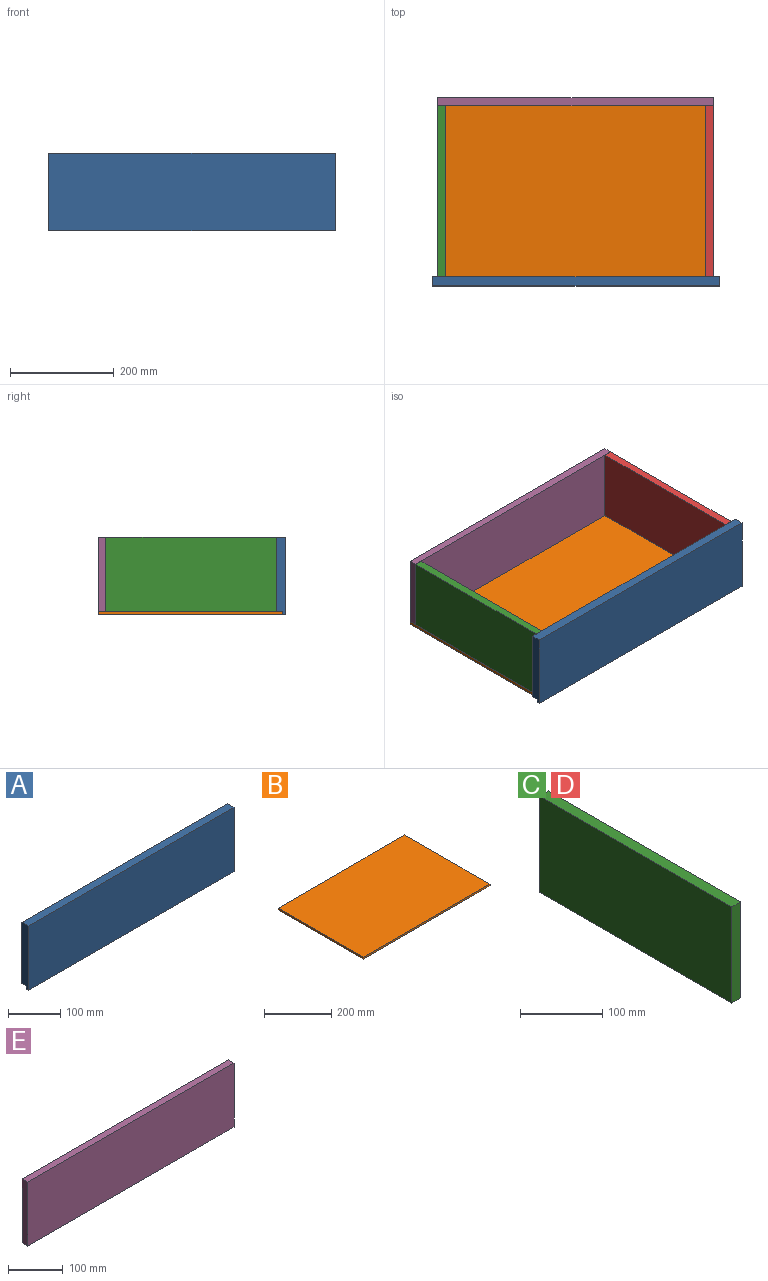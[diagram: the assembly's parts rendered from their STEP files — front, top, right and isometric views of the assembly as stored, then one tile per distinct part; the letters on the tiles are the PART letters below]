
ASSEMBLY  parts=5 mates=4
PART A: 8 faces, bbox 554x18x150 mm
  f0: plane 554x143mm, normal (0,1,0), area 79222mm2, adj f1,f2,f4,f6
  f1: plane 554x18mm, normal (0,0,1), area 9972mm2, adj f0,f2,f4,f5
  f2: plane 150x18mm, normal (-1,0,0), area 2616mm2, adj f0,f1,f3,f5,f6,f7
  f3: plane 554x6mm, normal (0,0,-1), area 3324mm2, adj f2,f4,f5,f7
  f4: plane 150x18mm, normal (1,0,0), area 2616mm2, adj f0,f1,f3,f5,f6,f7
  f5: plane 554x150mm, normal (0,-1,0), area 83100mm2, adj f1,f2,f3,f4
  f6: plane 554x12mm, normal (0,0,-1), area 6648mm2, adj f0,f2,f4,f7
  f7: plane 554x7mm, normal (0,1,0), area 3878mm2, adj f2,f3,f4,f6
PART B: 6 faces, bbox 532.5x357x6.5 mm
  f0: plane 532.5x6.5mm, normal (0,1,0), area 3461.2mm2, adj f1,f3,f4,f5
  f1: plane 357x6.5mm, normal (-1,0,0), area 2320.5mm2, adj f0,f2,f4,f5
  f2: plane 532.5x6.5mm, normal (0,-1,0), area 3461.2mm2, adj f1,f3,f4,f5
  f3: plane 357x6.5mm, normal (1,0,0), area 2320.5mm2, adj f0,f2,f4,f5
  f4: plane 532.5x357mm, normal (0,0,1), area 190102.5mm2, adj f0,f1,f2,f3
  f5: plane 532.5x357mm, normal (0,0,-1), area 190102.5mm2, adj f0,f1,f2,f3
PART C: 6 faces, bbox 15x330x143 mm
  f0: plane 330x15mm, normal (0,0,1), area 4950mm2, adj f1,f3,f4,f5
  f1: plane 143x15mm, normal (0,-1,0), area 2145mm2, adj f0,f2,f4,f5
  f2: plane 330x15mm, normal (0,0,-1), area 4950mm2, adj f1,f3,f4,f5
  f3: plane 143x15mm, normal (0,1,0), area 2145mm2, adj f0,f2,f4,f5
  f4: plane 330x143mm, normal (1,0,0), area 47190mm2, adj f0,f1,f2,f3
  f5: plane 330x143mm, normal (-1,0,0), area 47190mm2, adj f0,f1,f2,f3
PART D: same geometry as C
PART E: 6 faces, bbox 532.5x15x143 mm
  f0: plane 532.5x15mm, normal (0,0,1), area 7987.5mm2, adj f1,f3,f4,f5
  f1: plane 143x15mm, normal (-1,0,0), area 2145mm2, adj f0,f2,f4,f5
  f2: plane 532.5x15mm, normal (0,0,-1), area 7987.5mm2, adj f1,f3,f4,f5
  f3: plane 143x15mm, normal (1,0,0), area 2145mm2, adj f0,f2,f4,f5
  f4: plane 532.5x143mm, normal (0,-1,0), area 76147.5mm2, adj f0,f1,f2,f3
  f5: plane 532.5x143mm, normal (0,1,0), area 76147.5mm2, adj f0,f1,f2,f3
PLACE A t=(-90.94,-286.05,-19.47)mm
PLACE B t=(-181.39,-122.94,-45.07)mm
PLACE C t=(-425.02,-10.88,-16.38)mm
PLACE D t=(92.48,-10.88,-16.38)mm
PLACE E t=(61.48,58.95,-49.34)mm
MATE fastened E.f2 <-> B.f4  axis (0,0,-1) through (107.48,58.95,-38.57)mm
MATE fastened C.f3 <-> E.f4  axis (0,1,0) through (-425.02,43.95,-38.57)mm
MATE fastened E.f4 <-> D.f3  axis (0,-1,0) through (107.48,43.95,-38.57)mm
MATE fastened A.f0 <-> D.f1  axis (0,1,0) through (119.18,-286.05,104.43)mm
